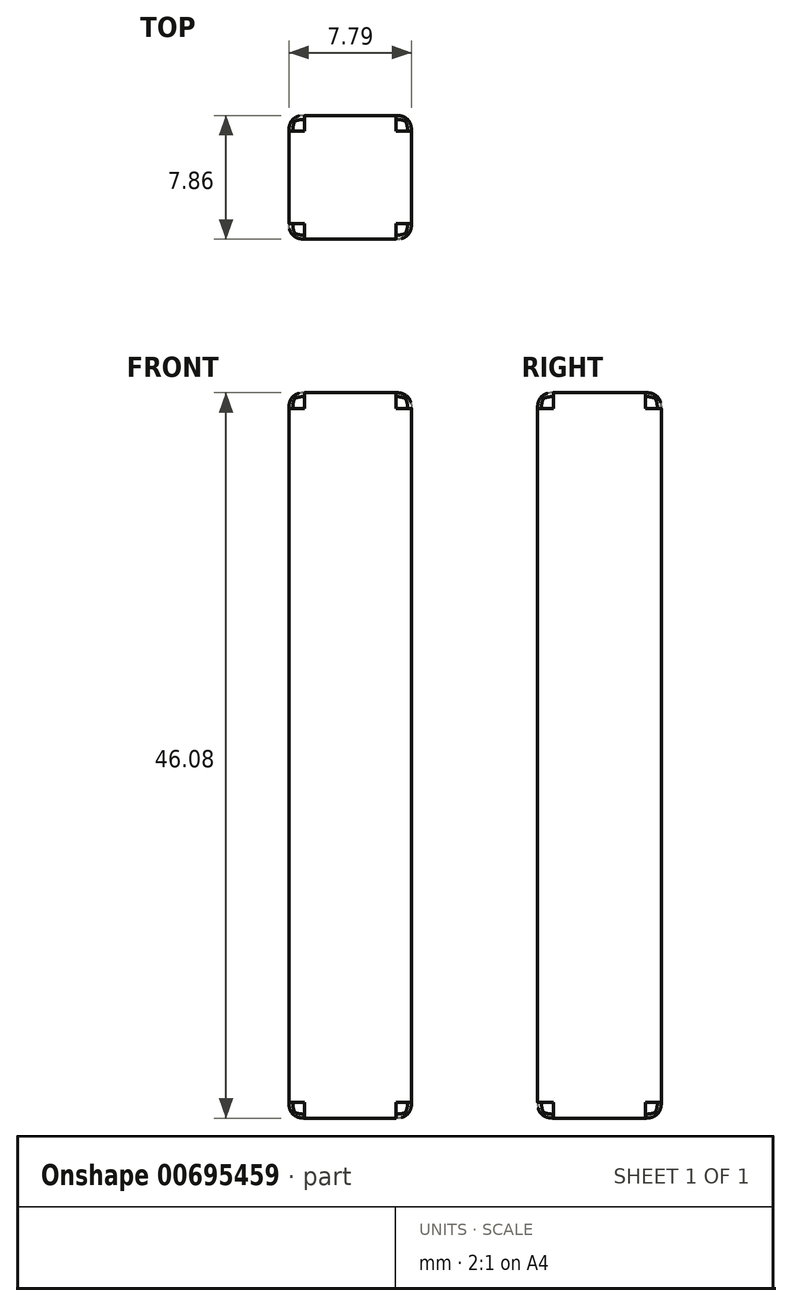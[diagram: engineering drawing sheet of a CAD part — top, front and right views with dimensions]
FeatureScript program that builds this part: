
annotation { "Feature Type Name" : "Feature", "Feature Type Description" : "" }
export const myFeature = defineFeature(function(context is Context, id is Id, definition is map)
    precondition{}
    {
        {
            var Q0;
            Q0=qCreatedBy(makeId("Top.planeOp"),FACE);
            var sketch = newSketch(context, id + "F0", { "sketchPlane" : qUnion([Q0])});
            skLineSegment(sketch, "E0.bottom", {"start": v(-49.54, -28.88) * mm, "end": v(-41.75, -28.88) * mm});
            skLineSegment(sketch, "E0.top", {"start": v(-49.54, -36.74) * mm, "end": v(-41.75, -36.74) * mm});
            skLineSegment(sketch, "E0.left", {"start": v(-49.54, -28.88) * mm, "end": v(-49.54, -36.74) * mm});
            skLineSegment(sketch, "E0.right", {"start": v(-41.75, -28.88) * mm, "end": v(-41.75, -36.74) * mm});
            skSolve(sketch);
        }
        {
            var Q0;
            Q0=makeQuery(id+"F0.imprint","IMPRINT",FACE,{"disambiguationData":[TD([[makeQuery(id+"F0.imprint","IMPRINT",EDGE,{"derivedFrom":sQuery(id+"F0.wireOp",EDGE,"E0.bottom")}),-1.0]])]});
            extrude(context, id + "F1", {"entities" : qUnion([Q0]), "depth" : 46.08 * mm, "offsetDistance" : 25.4 * mm});
        }
        {
            var Q0;
            Q0=makeQuery(id+"F1.opExtrude","SWEPT_EDGE",EDGE,{"disambiguationData":[OSD([sQuery(id+"F0.wireOp",EDGE,"E0.top"),sQuery(id+"F0.wireOp",EDGE,"E0.right")])]});
            var Q1;
            Q1=makeQuery(id+"F1.opExtrude","CAP_FACE",FACE,{"disambiguationData":[OSD([sQuery(id+"F0.wireOp",EDGE,"E0.bottom"),sQuery(id+"F0.wireOp",EDGE,"E0.top"),sQuery(id+"F0.wireOp",EDGE,"E0.left"),sQuery(id+"F0.wireOp",EDGE,"E0.right")])],"isStart":false});
            var Q2;
            Q2=makeQuery(id+"F1.opExtrude","SWEPT_EDGE",EDGE,{"disambiguationData":[OSD([sQuery(id+"F0.wireOp",EDGE,"E0.top"),sQuery(id+"F0.wireOp",EDGE,"E0.left")])]});
            var Q3;
            Q3=makeQuery(id+"F1.opExtrude","CAP_FACE",FACE,{"disambiguationData":[OSD([sQuery(id+"F0.wireOp",EDGE,"E0.bottom"),sQuery(id+"F0.wireOp",EDGE,"E0.top"),sQuery(id+"F0.wireOp",EDGE,"E0.left"),sQuery(id+"F0.wireOp",EDGE,"E0.right")])],"isStart":true});
            var Q4;
            Q4=makeQuery(id+"F1.opExtrude","SWEPT_EDGE",EDGE,{"disambiguationData":[OSD([sQuery(id+"F0.wireOp",EDGE,"E0.bottom"),sQuery(id+"F0.wireOp",EDGE,"E0.right")])]});
            var Q5;
            Q5=makeQuery(id+"F1.opExtrude","SWEPT_FACE",FACE,{"disambiguationData":[OSD([sQuery(id+"F0.wireOp",EDGE,"E0.bottom")])]});
            var Q6;
            Q6=makeQuery(id+"F1.opExtrude","SWEPT_FACE",FACE,{"disambiguationData":[OSD([sQuery(id+"F0.wireOp",EDGE,"E0.top")])]});
            var Q7;
            Q7=makeQuery(id+"F1.opExtrude","SWEPT_FACE",FACE,{"disambiguationData":[OSD([sQuery(id+"F0.wireOp",EDGE,"E0.left")])]});
            var Q8;
            Q8=makeQuery(id+"F1.opExtrude","SWEPT_FACE",FACE,{"disambiguationData":[OSD([sQuery(id+"F0.wireOp",EDGE,"E0.right")])]});
            var Q9;
            Q9=makeQuery(id+"F1.opExtrude","SWEPT_EDGE",EDGE,{"disambiguationData":[OSD([sQuery(id+"F0.wireOp",EDGE,"E0.bottom"),sQuery(id+"F0.wireOp",EDGE,"E0.left")])]});
            var Q10;
            Q10=makeQuery(id+"F1.opExtrude","CAP_EDGE",EDGE,{"disambiguationData":[OSD([sQuery(id+"F0.wireOp",EDGE,"E0.bottom")])],"isStart":true});
            var Q11;
            Q11=makeQuery(id+"F1.opExtrude","CAP_EDGE",EDGE,{"disambiguationData":[OSD([sQuery(id+"F0.wireOp",EDGE,"E0.bottom")])],"isStart":false});
            var Q12;
            Q12=makeQuery(id+"F1.opExtrude","CAP_EDGE",EDGE,{"disambiguationData":[OSD([sQuery(id+"F0.wireOp",EDGE,"E0.top")])],"isStart":false});
            var Q13;
            Q13=makeQuery(id+"F1.opExtrude","CAP_EDGE",EDGE,{"disambiguationData":[OSD([sQuery(id+"F0.wireOp",EDGE,"E0.left")])],"isStart":false});
            var Q14;
            Q14=makeQuery(id+"F1.opExtrude","CAP_EDGE",EDGE,{"disambiguationData":[OSD([sQuery(id+"F0.wireOp",EDGE,"E0.left")])],"isStart":true});
            var Q15;
            Q15=makeQuery(id+"F1.opExtrude","CAP_EDGE",EDGE,{"disambiguationData":[OSD([sQuery(id+"F0.wireOp",EDGE,"E0.right")])],"isStart":true});
            var Q16;
            Q16=makeQuery(id+"F1.opExtrude","CAP_EDGE",EDGE,{"disambiguationData":[OSD([sQuery(id+"F0.wireOp",EDGE,"E0.right")])],"isStart":false});
            var Q17;
            Q17=makeQuery(id+"F1.opExtrude","CAP_EDGE",EDGE,{"disambiguationData":[OSD([sQuery(id+"F0.wireOp",EDGE,"E0.top")])],"isStart":true});
            fillet(context, id + "F2", {"entities" : qUnion([Q0, Q1, Q2, Q3, Q4, Q5, Q6, Q7, Q8, Q9, Q10, Q11, Q12, Q13, Q14, Q15, Q16, Q17]), "radius" : 1 * mm, "tangentPropagation" : true, "rho" : 0.5, "crossSection" : FilletCrossSection.CONIC, "allowEdgeOverflow" : false});
        }
    });
